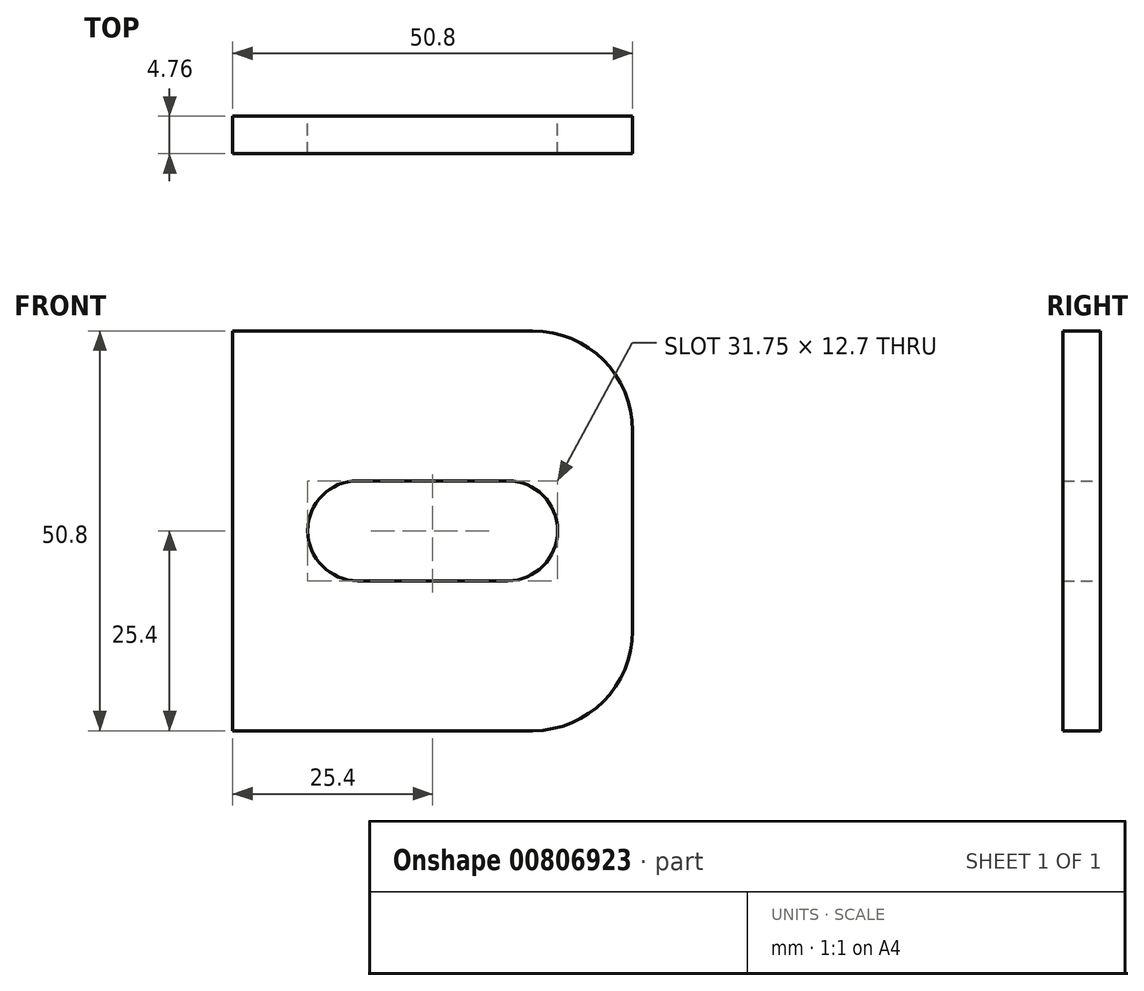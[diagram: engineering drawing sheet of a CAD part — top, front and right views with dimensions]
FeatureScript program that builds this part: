
annotation { "Feature Type Name" : "Feature", "Feature Type Description" : "" }
export const myFeature = defineFeature(function(context is Context, id is Id, definition is map)
    precondition{}
    {
        {
            var Q0;
            Q0=qCreatedBy(makeId("Front.planeOp"),FACE);
            var sketch = newSketch(context, id + "F0", { "sketchPlane" : qUnion([Q0])});
            skLineSegment(sketch, "E0.bottom", {"start": v(0, 0) * mm, "end": v(38.1, 0) * mm});
            skLineSegment(sketch, "E0.top", {"start": v(0, 50.8) * mm, "end": v(38.1, 50.8) * mm});
            skLineSegment(sketch, "E0.left", {"start": v(0, 0) * mm, "end": v(0, 50.8) * mm});
            skLineSegment(sketch, "E0.right", {"start": v(50.8, 12.7) * mm, "end": v(50.8, 38.1) * mm});
            skPoint(sketch, "E1.startSnap0", {"position": v(0, 25.4) * mm});
            skArc(sketch, "E2.0.startCap", {"start": v(15.87, 19.05) * mm, "mid": v(9.52, 25.4) * mm, "end": v(15.87, 31.75) * mm});
            skArc(sketch, "E2.0.endCap", {"start": v(34.92, 31.75) * mm, "mid": v(41.27, 25.4) * mm, "end": v(34.92, 19.05) * mm});
            skLineSegment(sketch, "E2.0.left", {"start": v(15.87, 31.75) * mm, "end": v(34.92, 31.75) * mm});
            skLineSegment(sketch, "E2.0.right", {"start": v(15.87, 19.05) * mm, "end": v(34.92, 19.05) * mm});
            skPoint(sketch, "E3.visualSharp", {"position": v(50.8, 50.8) * mm});
            skArc(sketch, "E3.filletArc", {"start": v(50.8, 38.1) * mm, "mid": v(47.08, 47.08) * mm, "end": v(38.1, 50.8) * mm});
            skPoint(sketch, "E4.visualSharp", {"position": v(50.8, 0) * mm});
            skArc(sketch, "E4.filletArc", {"start": v(38.1, 0) * mm, "mid": v(47.08, 3.72) * mm, "end": v(50.8, 12.7) * mm});
            skSolve(sketch);
        }
        {
            var Q0;
            Q0=qSketchRegion(id+"F0",true);
            extrude(context, id + "F1", {"entities" : qUnion([Q0]), "depth" : 4.76 * mm, "offsetDistance" : 25.4 * mm});
        }
    });
